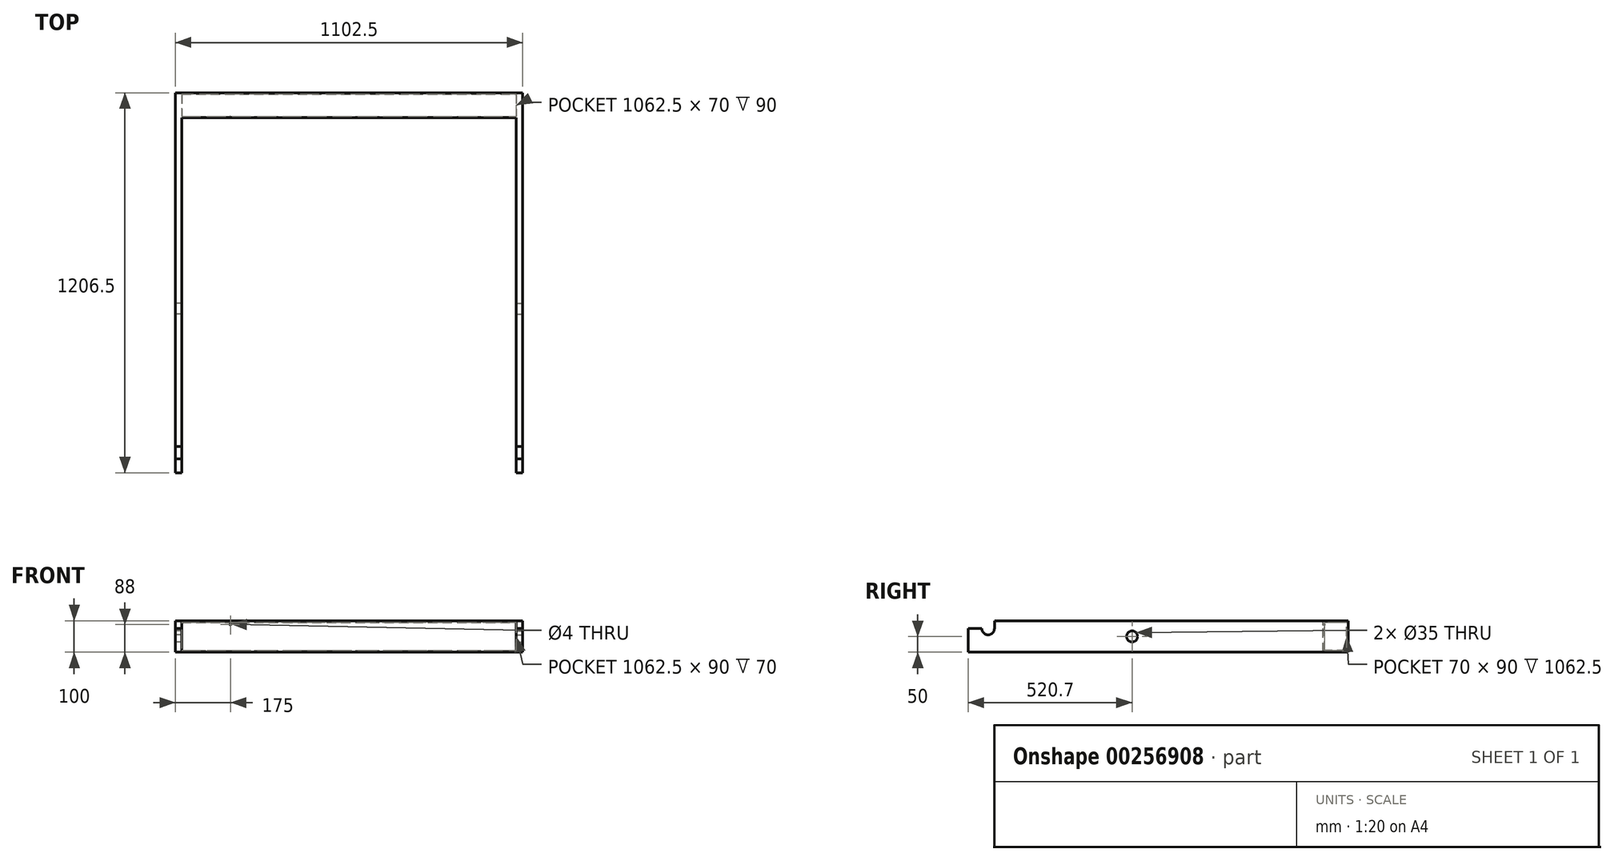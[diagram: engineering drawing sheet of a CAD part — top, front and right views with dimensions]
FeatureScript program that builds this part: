
annotation { "Feature Type Name" : "Feature", "Feature Type Description" : "" }
export const myFeature = defineFeature(function(context is Context, id is Id, definition is map)
    precondition{}
    {
        {
            var Q0;
            Q0=qCreatedBy(makeId("Right.planeOp"),FACE);
            var sketch = newSketch(context, id + "F0", { "sketchPlane" : qUnion([Q0])});
            skLineSegment(sketch, "E0.bottom", {"start": v(0, 0) * mm, "end": v(-1206.5, 0) * mm});
            skLineSegment(sketch, "E0.top", {"start": v(0, 100) * mm, "end": v(-1123, 100) * mm});
            skLineSegment(sketch, "E0.left", {"start": v(0, 0) * mm, "end": v(0, 100) * mm});
            skLineSegment(sketch, "E0.right", {"start": v(-1206.5, 0) * mm, "end": v(-1206.5, 75) * mm});
            skPoint(sketch, "E1", {"position": v(-685.8, 100) * mm});
            skPoint(sketch, "E2", {"position": v(-1143, 100) * mm});
            skCircle(sketch, "E3", {"center": v(-685.8, 50) * mm, "radius": 17.5 * mm});
            skArc(sketch, "E4", {"start": v(-1163, 75) * mm, "mid": v(-1143, 55) * mm, "end": v(-1123, 75) * mm});
            skLineSegment(sketch, "E5", {"start": v(-1123, 100) * mm, "end": v(-1123, 75) * mm});
            skLineSegment(sketch, "E6", {"start": v(-1206.5, 75) * mm, "end": v(-1163, 75) * mm});
            skSolve(sketch);
        }
        {
            var Q0;
            Q0=makeQuery(id+"F0.imprint","IMPRINT",FACE,{"disambiguationData":[TD([[makeQuery(id+"F0.imprint","IMPRINT",EDGE,{"derivedFrom":sQuery(id+"F0.wireOp",EDGE,"E0.bottom")}),-1.0]])]});
            extrude(context, id + "F1", {"entities" : qUnion([Q0]), "oppositeDirection" : true, "depth" : 20 * mm});
        }
        {
            var Q0;
            Q0=makeQuery(id+"F1.opExtrude","CAP_FACE",FACE,{"disambiguationData":[OSD([sQuery(id+"F0.wireOp",EDGE,"E0.bottom"),sQuery(id+"F0.wireOp",EDGE,"E0.top"),sQuery(id+"F0.wireOp",EDGE,"E0.left"),sQuery(id+"F0.wireOp",EDGE,"E0.right"),sQuery(id+"F0.wireOp",EDGE,"qeFhqNGE-qipG-TgRW-EqxA-nLF9aQ86EUaH"),sQuery(id+"F0.wireOp",EDGE,"E3"),sQuery(id+"F0.wireOp",EDGE,"adbb26b5-c0e8-4679-b47e-b74efc70eab8.trimOffspring")])],"isStart":false});
            var sketch = newSketch(context, id + "F2", { "sketchPlane" : qUnion([Q0])});
            skLineSegment(sketch, "E7.bottom", {"start": v(0, 0) * mm, "end": v(80, 0) * mm});
            skLineSegment(sketch, "E7.top", {"start": v(0, 100) * mm, "end": v(80, 100) * mm});
            skLineSegment(sketch, "E7.left", {"start": v(0, 0) * mm, "end": v(0, 100) * mm});
            skLineSegment(sketch, "E7.right", {"start": v(80, 0) * mm, "end": v(80, 100) * mm});
            skLineSegment(sketch, "E8.0", {"start": v(5, 95) * mm, "end": v(75, 95) * mm});
            skLineSegment(sketch, "E8.1", {"start": v(5, 5) * mm, "end": v(5, 95) * mm});
            skLineSegment(sketch, "E8.2", {"start": v(5, 5) * mm, "end": v(75, 5) * mm});
            skLineSegment(sketch, "E8.3", {"start": v(75, 5) * mm, "end": v(75, 95) * mm});
            skSolve(sketch);
        }
        {
            var Q0;
            Q0=makeQuery(id+"F2.imprint","IMPRINT",FACE,{"disambiguationData":[TD([[makeQuery(id+"F2.imprint","IMPRINT",EDGE,{"derivedFrom":sQuery(id+"F2.wireOp",EDGE,"E7.bottom")}),1.0]])]});
            extrude(context, id + "F3", {"entities" : qUnion([Q0]), "operationType" : NewBodyOperationType.ADD, "depth" : 1062.5 * mm});
        }
        {
            var Q0;
            {var subQ0=sQuery(id+"F0.wireOp",EDGE,"qeFhqNGE-qipG-TgRW-EqxA-nLF9aQ86EUaH");var subQ1=sQuery(id+"F0.wireOp",EDGE,"E0.right");var subQ2=sQuery(id+"F0.wireOp",EDGE,"E0.top");var subQ3=sQuery(id+"F0.wireOp",EDGE,"E0.bottom");var subQ4=sQuery(id+"F0.wireOp",EDGE,"E3");var subQ5=sQuery(id+"F0.wireOp",EDGE,"adbb26b5-c0e8-4679-b47e-b74efc70eab8.trimOffspring");Q0=makeQuery(id+"F3.boolean.opBoolean","SPLIT",FACE,{"disambiguationData":[TD([makeQuery(id+"F1.opExtrude","SWEPT_FACE",FACE,{"disambiguationData":[OSD([subQ3])]})])],"derivedFrom":makeQuery(id+"F1.opExtrude","CAP_FACE",FACE,{"disambiguationData":[OSD([subQ3,subQ2,sQuery(id+"F0.wireOp",EDGE,"E0.left"),subQ1,subQ0,subQ4,subQ5])],"isStart":false})});}
            cPlane(context, id + "F4", {"entities" : qUnion([Q0]), "cplaneType" : CPlaneType.OFFSET, "offset" : 531.25 * mm, "width" : 152.4 * mm, "height" : 152.4 * mm});
        }
        {
            var Q0;
            Q0=makeQuery(id+"F1.opExtrude","SWEPT_BODY",BODY,{"disambiguationData":[OSD([sQuery(id+"F0.wireOp",EDGE,"E0.bottom"),sQuery(id+"F0.wireOp",EDGE,"E0.top"),sQuery(id+"F0.wireOp",EDGE,"E0.left"),sQuery(id+"F0.wireOp",EDGE,"E0.right"),sQuery(id+"F0.wireOp",EDGE,"qeFhqNGE-qipG-TgRW-EqxA-nLF9aQ86EUaH"),sQuery(id+"F0.wireOp",EDGE,"E3"),sQuery(id+"F0.wireOp",EDGE,"adbb26b5-c0e8-4679-b47e-b74efc70eab8.trimOffspring")])]});
            var Q1;
            Q1=qCreatedBy(id+"F4.planeOp",FACE);
            mirror(context, id + "F5", {"operationType" : NewBodyOperationType.ADD, "entities" : qUnion([Q0]), "mirrorPlane" : qUnion([Q1])});
        }
        {
            var Q0;
            Q0=makeQuery(id+"F3.opExtrude","SWEPT_FACE",FACE,{"disambiguationData":[OSD([sQuery(id+"F2.wireOp",EDGE,"E7.right")])]});
            var sketch = newSketch(context, id + "F6", { "sketchPlane" : qUnion([Q0])});
            skCircle(sketch, "E9", {"center": v(-927.5, 88) * mm, "radius": 2 * mm});
            skPoint(sketch, "E9.centerSnap0", {"position": v(-1082.5, 50) * mm});
            skSolve(sketch);
        }
        {
            var Q0;
            Q0 = qSketchRegion(id + "F6", true);
            extrude(context, id + "F7", {"entities" : qUnion([Q0]), "operationType" : NewBodyOperationType.REMOVE, "endBound" : BoundingType.UP_TO_NEXT, "oppositeDirection" : true, "depth" : 25.4 * mm});
        }
    });
